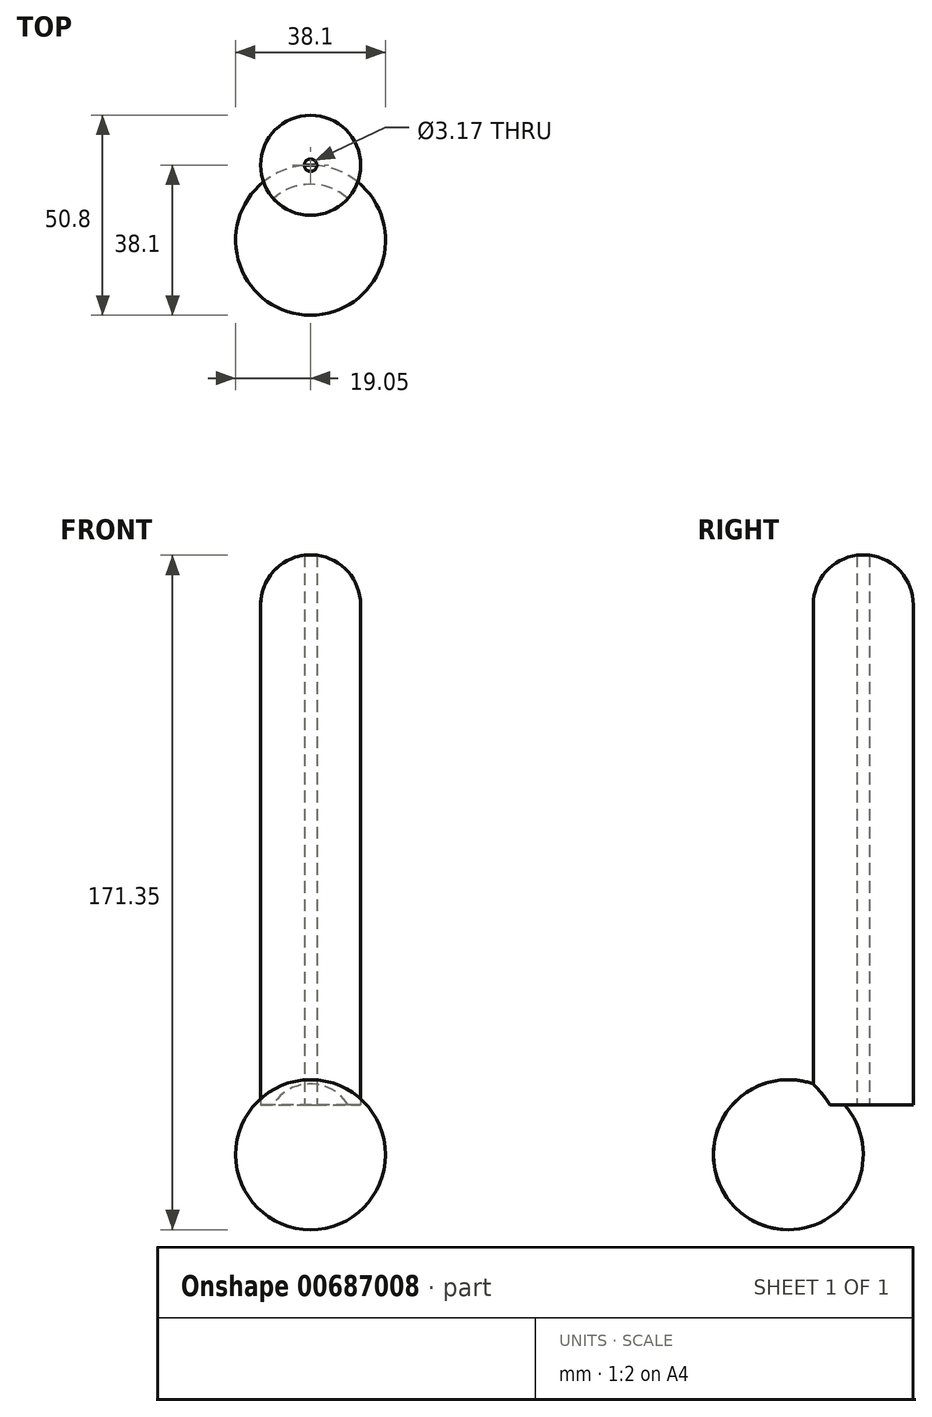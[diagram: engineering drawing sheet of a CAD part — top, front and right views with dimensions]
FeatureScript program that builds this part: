
annotation { "Feature Type Name" : "Feature", "Feature Type Description" : "" }
export const myFeature = defineFeature(function(context is Context, id is Id, definition is map)
    precondition{}
    {
        {
            var Q0;
            Q0=qCreatedBy(makeId("Front.planeOp"),FACE);
            var sketch = newSketch(context, id + "F0", { "sketchPlane" : qUnion([Q0])});
            skLineSegment(sketch, "E0", {"start": v(0, 0) * mm, "end": v(0, 127) * mm});
            skLineSegment(sketch, "E1", {"start": v(-12.7, 127) * mm, "end": v(-12.7, 0) * mm});
            skArc(sketch, "E2", {"start": v(0, 139.7) * mm, "mid": v(-8.98, 135.98) * mm, "end": v(-12.7, 127) * mm});
            skLineSegment(sketch, "E3", {"start": v(0, 139.7) * mm, "end": v(0, 127) * mm});
            skLineSegment(sketch, "E4", {"start": v(-12.7, 0) * mm, "end": v(0, 0) * mm});
            skSolve(sketch);
        }
        {
            var Q0;
            Q0 = qSketchRegion(id + "F0", true);
            var Q1;
            Q1=sQuery(id+"F0.wireOp",EDGE,"E0");
            revolve(context, id + "F1", {"entities" : qUnion([Q0]), "axis" : qUnion([Q1]), "revolveType" : RevolveType.FULL});
        }
        {
            var Q0;
            Q0=makeQuery(id+"F1.opRevolve","SWEPT_FACE",FACE,{"disambiguationData":[OSD([sQuery(id+"F0.wireOp",EDGE,"E4")])]});
            var sketch = newSketch(context, id + "F2", { "sketchPlane" : qUnion([Q0])});
            skCircle(sketch, "E5", {"center": v(0, 0) * mm, "radius": 1.59 * mm});
            skSolve(sketch);
        }
        {
            var Q0;
            Q0 = qSketchRegion(id + "F2", true);
            extrude(context, id + "F3", {"entities" : qUnion([Q0]), "operationType" : NewBodyOperationType.REMOVE, "endBound" : BoundingType.THROUGH_ALL, "oppositeDirection" : true, "depth" : 25.4 * mm, "offsetDistance" : 25.4 * mm});
        }
        {
            var Q0;
            Q0=qCreatedBy(makeId("Right.planeOp"),FACE);
            var sketch = newSketch(context, id + "F4", { "sketchPlane" : qUnion([Q0])});
            skPoint(sketch, "E6.center.orphan", {"position": v(0, -12.7) * mm});
            skArc(sketch, "E7", {"start": v(-19.05, -31.75) * mm, "mid": v(0, -12.7) * mm, "end": v(-19.05, 6.35) * mm});
            skLineSegment(sketch, "E8", {"start": v(-19.05, 6.35) * mm, "end": v(-19.05, -12.7) * mm});
            skLineSegment(sketch, "E9", {"start": v(-19.05, -12.7) * mm, "end": v(-19.05, -31.75) * mm});
            skLineSegment(sketch, "E10", {"start": v(0, 0) * mm, "end": v(0, -12.7) * mm});
            skPoint(sketch, "E11.MirrorCS.end.orphan", {"position": v(-38.1, -12.7) * mm});
            skPoint(sketch, "E11.MirrorCS.start.orphan", {"position": v(-38.1, 0) * mm});
            skPoint(sketch, "E12.orphan", {"position": v(-19.05, -31.75) * mm});
            skPoint(sketch, "E13.orphan", {"position": v(-19.05, 6.35) * mm});
            skPoint(sketch, "E14.MirrorCS.end.orphan", {"position": v(19.05, -12.7) * mm});
            skPoint(sketch, "E14.MirrorCS.start.orphan", {"position": v(19.05, 6.35) * mm});
            skPoint(sketch, "E15.MirrorCS.end.orphan", {"position": v(19.05, -31.75) * mm});
            skSolve(sketch);
        }
        {
            var Q0;
            Q0 = qSketchRegion(id + "F4", true);
            var Q1;
            Q1=sQuery(id+"F4.wireOp",EDGE,"E9");
            revolve(context, id + "F5", {"operationType" : NewBodyOperationType.ADD, "entities" : qUnion([Q0]), "axis" : qUnion([Q1]), "revolveType" : RevolveType.FULL});
        }
    });
